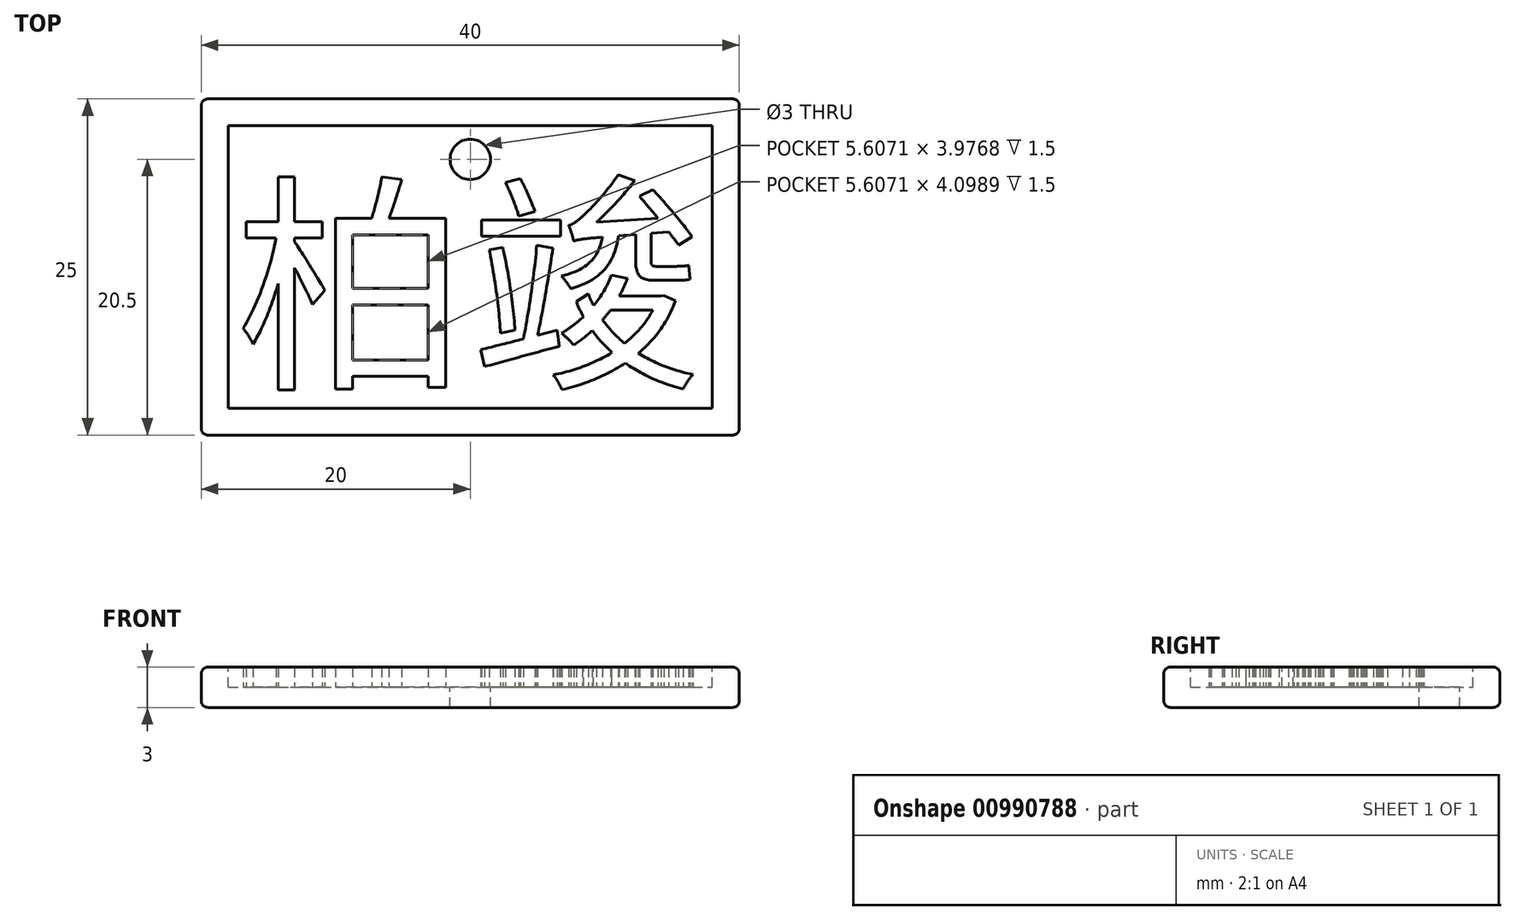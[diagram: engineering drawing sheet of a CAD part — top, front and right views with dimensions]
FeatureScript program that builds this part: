
annotation { "Feature Type Name" : "Feature", "Feature Type Description" : "" }
export const myFeature = defineFeature(function(context is Context, id is Id, definition is map)
    precondition{}
    {
        {
            var Q0;
            Q0=qCreatedBy(makeId("Top.planeOp"),FACE);
            var sketch = newSketch(context, id + "F0", { "sketchPlane" : qUnion([Q0])});
            skLineSegment(sketch, "E0.bottom", {"start": v(20, -12.5) * mm, "end": v(-20, -12.5) * mm});
            skLineSegment(sketch, "E0.top", {"start": v(20, 12.5) * mm, "end": v(-20, 12.5) * mm});
            skLineSegment(sketch, "E0.left", {"start": v(20, -12.5) * mm, "end": v(20, 12.5) * mm});
            skLineSegment(sketch, "E0.right", {"start": v(-20, -12.5) * mm, "end": v(-20, 12.5) * mm});
            skPoint(sketch, "E0.middle", {"position": v(0, 0) * mm});
            skSolve(sketch);
        }
        {
            var Q0;
            Q0 = qSketchRegion(id + "F0", true);
            extrude(context, id + "F1", {"entities" : qUnion([Q0]), "depth" : 3 * mm, "offsetDistance" : 25 * mm});
        }
        {
            var Q0;
            Q0=makeQuery(id+"F1.opExtrude","CAP_FACE",FACE,{"disambiguationData":[OSD([sQuery(id+"F0.wireOp",EDGE,"E0.bottom"),sQuery(id+"F0.wireOp",EDGE,"E0.top"),sQuery(id+"F0.wireOp",EDGE,"E0.left"),sQuery(id+"F0.wireOp",EDGE,"E0.right")])],"isStart":false});
            var sketch = newSketch(context, id + "F2", { "sketchPlane" : qUnion([Q0])});
            skLineSegment(sketch, "E1.0", {"start": v(18, -10.5) * mm, "end": v(18, 10.5) * mm});
            skLineSegment(sketch, "E1.1", {"start": v(-18, -10.5) * mm, "end": v(18, -10.5) * mm});
            skLineSegment(sketch, "E1.2", {"start": v(-18, 10.5) * mm, "end": v(-18, -10.5) * mm});
            skLineSegment(sketch, "E1.3", {"start": v(18, 10.5) * mm, "end": v(-18, 10.5) * mm});
            skSolve(sketch);
        }
        {
            var Q0;
            Q0=makeQuery(id+"F2.imprint","IMPRINT",FACE,{"disambiguationData":[TD([[makeQuery(id+"F2.imprint","IMPRINT",EDGE,{"derivedFrom":sQuery(id+"F2.wireOp",EDGE,"E1.0")}),1.0]])]});
            extrude(context, id + "F3", {"entities" : qUnion([Q0]), "operationType" : NewBodyOperationType.REMOVE, "oppositeDirection" : true, "depth" : 1.5 * mm, "offsetDistance" : 25 * mm});
        }
        {
            var Q0;
            Q0=makeQuery(id+"F3.boolean.opBoolean","COPY",FACE,{"derivedFrom":makeQuery(id+"F3.opExtrude","CAP_FACE",FACE,{"disambiguationData":[OSD([sQuery(id+"F2.wireOp",EDGE,"E1.0"),sQuery(id+"F2.wireOp",EDGE,"E1.1"),sQuery(id+"F2.wireOp",EDGE,"E1.2"),sQuery(id+"F2.wireOp",EDGE,"E1.3")])],"isStart":false})});
            var sketch = newSketch(context, id + "F4", { "sketchPlane" : qUnion([Q0])});
            skCircle(sketch, "E2", {"center": v(0, 8) * mm, "radius": 1.5 * mm});
            skSolve(sketch);
        }
        {
            var Q0;
            Q0 = qSketchRegion(id + "F4", true);
            extrude(context, id + "F5", {"entities" : qUnion([Q0]), "operationType" : NewBodyOperationType.REMOVE, "endBound" : BoundingType.THROUGH_ALL, "oppositeDirection" : true, "depth" : 25 * mm, "offsetDistance" : 25 * mm});
        }
        {
            var Q0;
            Q0=makeQuery(id+"F3.boolean.opBoolean","COPY",FACE,{"derivedFrom":makeQuery(id+"F3.opExtrude","CAP_FACE",FACE,{"disambiguationData":[OSD([sQuery(id+"F2.wireOp",EDGE,"E1.0"),sQuery(id+"F2.wireOp",EDGE,"E1.1"),sQuery(id+"F2.wireOp",EDGE,"E1.2"),sQuery(id+"F2.wireOp",EDGE,"E1.3")])],"isStart":false})});
            var sketch = newSketch(context, id + "F6", { "sketchPlane" : qUnion([Q0])});
            skText(sketch, "E3", { "text": "柏竣", "fontName": "NotoSansCJKtc-Regular.otf"});
            skPoint(sketch, "E4", {"position": v(0, -1.55) * mm});
            const initialGuessF6  = {"E3": [-0.0175, -0.0078, 1, 0, 0.0125]};
            skSetInitialGuess(sketch, initialGuessF6);
            skSolve(sketch);
        }
        {
            var Q0;
            Q0 = qSketchRegion(id + "F6", true);
            extrude(context, id + "F7", {"entities" : qUnion([Q0]), "operationType" : NewBodyOperationType.ADD, "depth" : 1.5 * mm, "offsetDistance" : 25 * mm});
        }
        {
            var Q0;
            Q0=makeQuery(id+"F1.opExtrude","SWEPT_FACE",FACE,{"disambiguationData":[OSD([sQuery(id+"F0.wireOp",EDGE,"E0.bottom")])]});
            var Q1;
            Q1=makeQuery(id+"F1.opExtrude","SWEPT_FACE",FACE,{"disambiguationData":[OSD([sQuery(id+"F0.wireOp",EDGE,"E0.right")])]});
            var Q2;
            Q2=makeQuery(id+"F1.opExtrude","SWEPT_FACE",FACE,{"disambiguationData":[OSD([sQuery(id+"F0.wireOp",EDGE,"E0.left")])]});
            var Q3;
            Q3=makeQuery(id+"F1.opExtrude","SWEPT_FACE",FACE,{"disambiguationData":[OSD([sQuery(id+"F0.wireOp",EDGE,"E0.top")])]});
            fillet(context, id + "F8", {"entities" : qUnion([Q0, Q1, Q2, Q3]), "radius" : 0.5 * mm, "tangentPropagation" : true, "allowEdgeOverflow" : false});
        }
    });
